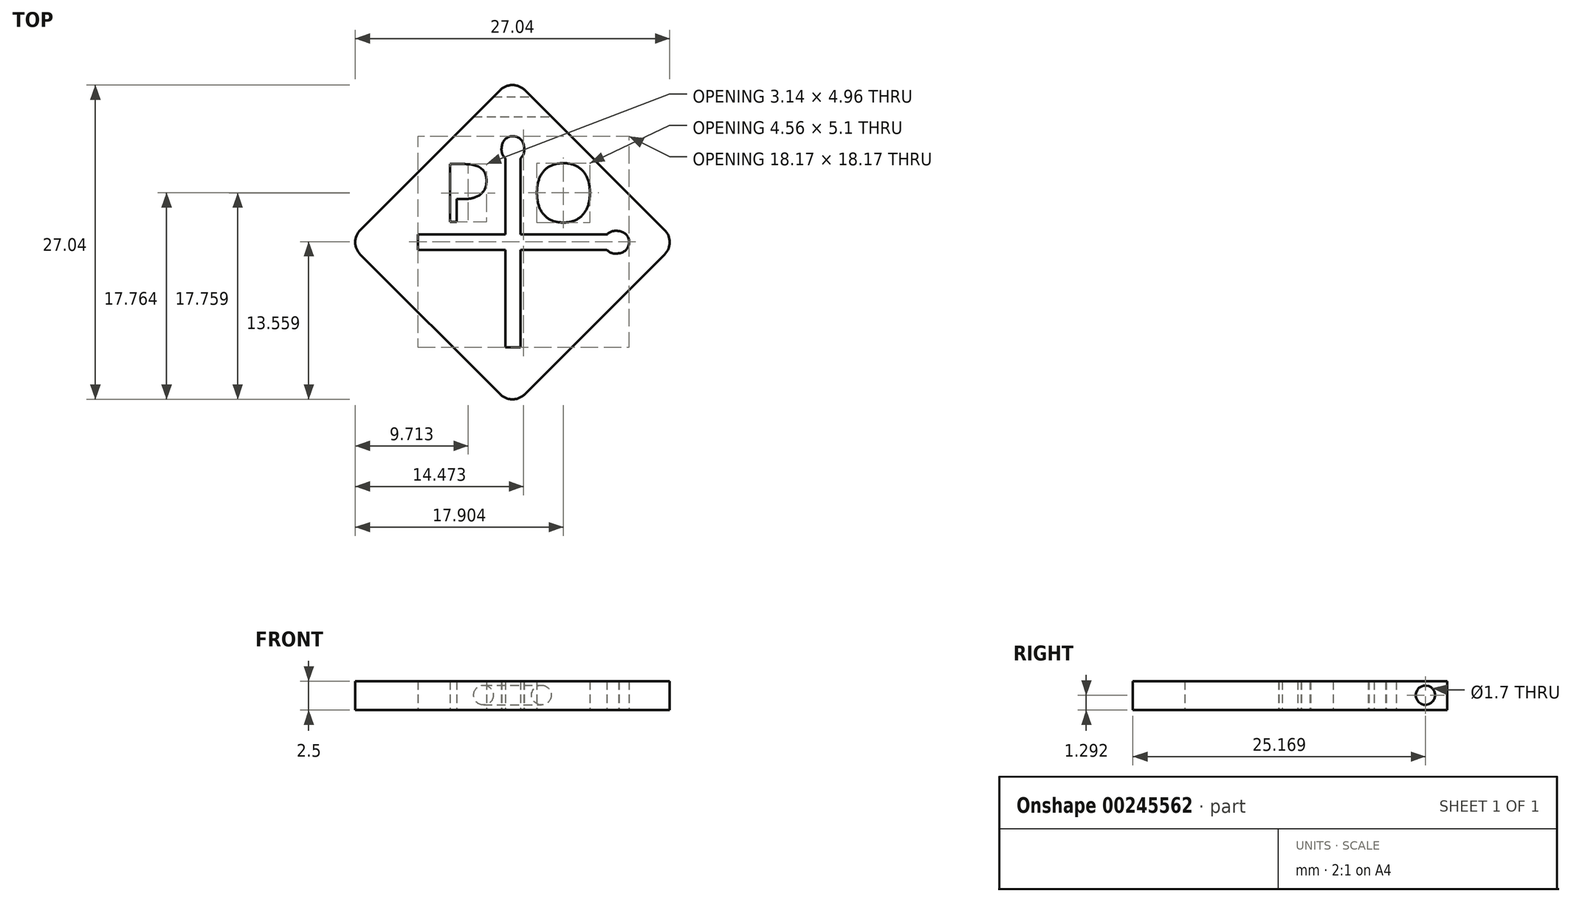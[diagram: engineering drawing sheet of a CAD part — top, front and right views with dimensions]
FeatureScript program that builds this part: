
annotation { "Feature Type Name" : "Feature", "Feature Type Description" : "" }
export const myFeature = defineFeature(function(context is Context, id is Id, definition is map)
    precondition{}
    {
        {
            var Q0;
            Q0=qCreatedBy(makeId("Top.planeOp"),FACE);
            var sketch = newSketch(context, id + "F0", { "sketchPlane" : qUnion([Q0])});
            skLineSegment(sketch, "E0", {"start": v(1.06, -1.06) * mm, "end": v(13.08, -13.08) * mm});
            skLineSegment(sketch, "E1", {"start": v(13.08, -15.2) * mm, "end": v(1.06, -27.22) * mm});
            skLineSegment(sketch, "E2", {"start": v(-1.06, -27.22) * mm, "end": v(-13.08, -15.2) * mm});
            skLineSegment(sketch, "E3", {"start": v(-13.08, -13.08) * mm, "end": v(-1.06, -1.06) * mm});
            skPoint(sketch, "E4.visualSharp", {"position": v(0, 0) * mm});
            skArc(sketch, "E4.filletArc", {"start": v(1.06, -1.06) * mm, "mid": v(0, -0.62) * mm, "end": v(-1.06, -1.06) * mm});
            skPoint(sketch, "E5.visualSharp", {"position": v(-14.14, -14.14) * mm});
            skArc(sketch, "E5.filletArc", {"start": v(-13.08, -13.08) * mm, "mid": v(-13.52, -14.14) * mm, "end": v(-13.08, -15.2) * mm});
            skPoint(sketch, "E6.visualSharp", {"position": v(14.14, -14.14) * mm});
            skArc(sketch, "E6.filletArc", {"start": v(13.08, -15.2) * mm, "mid": v(13.52, -14.14) * mm, "end": v(13.08, -13.08) * mm});
            skPoint(sketch, "E7.visualSharp", {"position": v(0, -28.28) * mm});
            skArc(sketch, "E7.filletArc", {"start": v(-1.06, -27.22) * mm, "mid": v(0, -27.66) * mm, "end": v(1.06, -27.22) * mm});
            skLineSegment(sketch, "E8", {"start": v(0, 0) * mm, "end": v(0, -31.86) * mm, "construction": true});
            skLineSegment(sketch, "E9", {"start": v(-14.14, -14.14) * mm, "end": v(14.14, -14.14) * mm, "construction": true});
            skLineSegment(sketch, "E10", {"start": v(-8.13, -13.48) * mm, "end": v(-8.13, -14.8) * mm});
            skLineSegment(sketch, "E11", {"start": v(-8.13, -14.8) * mm, "end": v(8.13, -14.8) * mm});
            skLineSegment(sketch, "E12", {"start": v(8.13, -13.48) * mm, "end": v(-8.13, -13.48) * mm});
            skLineSegment(sketch, "E13", {"start": v(-8.13, -13.48) * mm, "end": v(0, -13.48) * mm, "construction": true});
            skLineSegment(sketch, "E14", {"start": v(0, -13.48) * mm, "end": v(8.13, -13.48) * mm, "construction": true});
            skArc(sketch, "E15", {"start": v(9.18, -15.1) * mm, "mid": v(10.04, -14.12) * mm, "end": v(9.13, -13.2) * mm});
            skArc(sketch, "E16", {"start": v(9.13, -13.2) * mm, "mid": v(8.6, -13.2) * mm, "end": v(8.13, -13.48) * mm});
            skArc(sketch, "E17", {"start": v(8.13, -14.8) * mm, "mid": v(8.61, -15.1) * mm, "end": v(9.18, -15.1) * mm});
            skLineSegment(sketch, "E18", {"start": v(-0.62, -23.19) * mm, "end": v(0.7, -23.19) * mm});
            skLineSegment(sketch, "E19", {"start": v(0.7, -23.19) * mm, "end": v(0.7, -6.92) * mm});
            skLineSegment(sketch, "E20", {"start": v(-0.62, -6.92) * mm, "end": v(-0.62, -23.19) * mm});
            skLineSegment(sketch, "E21", {"start": v(-0.62, -23.19) * mm, "end": v(-0.62, -15.05) * mm, "construction": true});
            skLineSegment(sketch, "E22", {"start": v(-0.62, -15.05) * mm, "end": v(-0.62, -6.92) * mm, "construction": true});
            skArc(sketch, "E23", {"start": v(0.99, -5.88) * mm, "mid": v(0.02, -5.01) * mm, "end": v(-0.91, -5.92) * mm});
            skArc(sketch, "E24", {"start": v(-0.91, -5.92) * mm, "mid": v(-0.9, -6.46) * mm, "end": v(-0.62, -6.92) * mm});
            skArc(sketch, "E25", {"start": v(0.7, -6.92) * mm, "mid": v(1, -6.44) * mm, "end": v(0.99, -5.88) * mm});
            skText(sketch, "E26", { "text": "P\n", "fontName": "OpenSans-Regular.ttf"});
            skText(sketch, "E27", { "text": "O", "fontName": "OpenSans-Regular.ttf"});
            const initialGuessF0  = {"E26": [-0.00606, -0.01238, 1, 0, 0.005], "E27": [0.00168, -0.01238, 1, 0, 0.005]};
            skSetInitialGuess(sketch, initialGuessF0);
            skSolve(sketch);
        }
        {
            var Q0;
            Q0=makeQuery(id+"F0.imprint","IMPRINT",FACE,{"disambiguationData":[TD([[makeQuery(id+"F0.imprint","IMPRINT",EDGE,{"derivedFrom":sQuery(id+"F0.wireOp",EDGE,"E0")}),-1.0]])]});
            extrude(context, id + "F1", {"entities" : qUnion([Q0]), "depth" : 2.5 * mm});
        }
        {
            var Q0;
            Q0=qCreatedBy(makeId("Right.planeOp"),FACE);
            var sketch = newSketch(context, id + "F2", { "sketchPlane" : qUnion([Q0])});
            skCircle(sketch, "E28", {"center": v(-2.5, 1.3) * mm, "radius": 0.85 * mm});
            skSolve(sketch);
        }
        {
            var Q0;
            Q0=qSketchRegion(id+"F2",true);
            extrude(context, id + "F3", {"entities" : qUnion([Q0]), "operationType" : NewBodyOperationType.REMOVE, "endBound" : BoundingType.SYMMETRIC, "oppositeDirection" : true, "depth" : 25 * mm});
        }
    });
